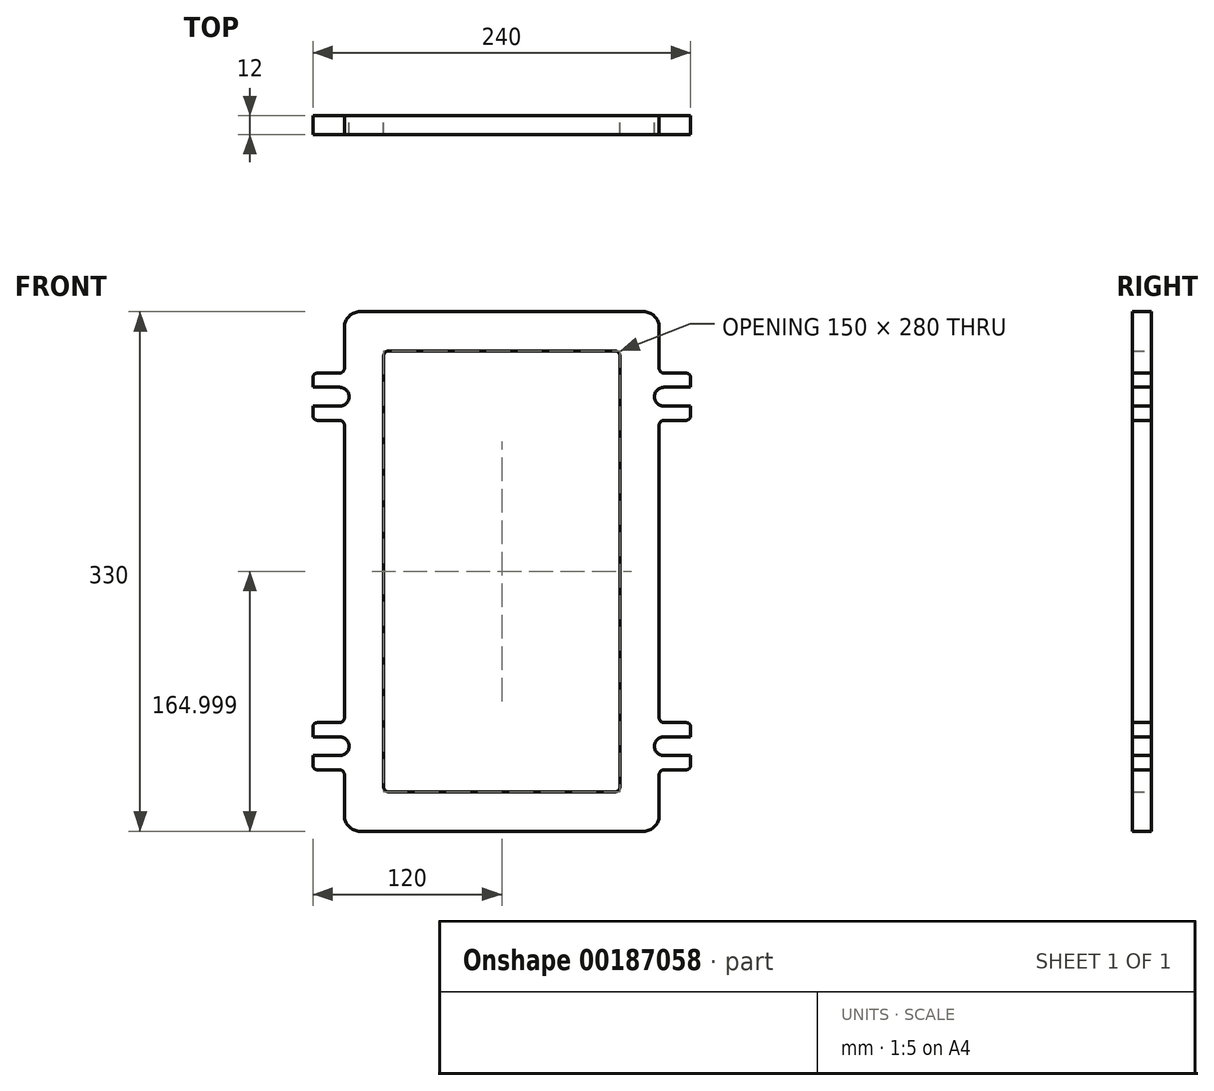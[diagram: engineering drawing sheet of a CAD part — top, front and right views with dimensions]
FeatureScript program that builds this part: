
annotation { "Feature Type Name" : "Feature", "Feature Type Description" : "" }
export const myFeature = defineFeature(function(context is Context, id is Id, definition is map)
    precondition{}
    {
        {
            var Q0;
            Q0=qCreatedBy(makeId("Front.planeOp"),FACE);
            var sketch = newSketch(context, id + "F0", { "sketchPlane" : qUnion([Q0])});
            skLineSegment(sketch, "E0", {"start": v(-100, 111.18) * mm, "end": v(0, 111.18) * mm});
            skLineSegment(sketch, "E1", {"start": v(-100, 111.18) * mm, "end": v(-100, 72.18) * mm});
            skLineSegment(sketch, "E2", {"start": v(-100, 72.18) * mm, "end": v(-120, 72.18) * mm});
            skLineSegment(sketch, "E3", {"start": v(-120, 72.18) * mm, "end": v(-120, 63.18) * mm});
            skLineSegment(sketch, "E4", {"start": v(-120, 63.18) * mm, "end": v(-103, 63.18) * mm});
            skLineSegment(sketch, "E5", {"start": v(-103, 51.18) * mm, "end": v(-120, 51.18) * mm});
            skLineSegment(sketch, "E6", {"start": v(-120, 51.18) * mm, "end": v(-120, 42.18) * mm});
            skLineSegment(sketch, "E7", {"start": v(-120, 42.18) * mm, "end": v(-100, 42.18) * mm});
            skLineSegment(sketch, "E8", {"start": v(-100, 42.18) * mm, "end": v(-100, -53.82) * mm});
            skArc(sketch, "E9", {"start": v(-103, 51.18) * mm, "mid": v(-97, 57.18) * mm, "end": v(-103, 63.18) * mm});
            skLineSegment(sketch, "E10.0", {"start": v(-75, 86.18) * mm, "end": v(0, 86.18) * mm});
            skLineSegment(sketch, "E11.0", {"start": v(-75, 86.18) * mm, "end": v(-75, -53.82) * mm});
            skLineSegment(sketch, "E12.MirrorCS", {"start": v(120, 51.18) * mm, "end": v(120, 42.18) * mm});
            skLineSegment(sketch, "E13.MirrorCS", {"start": v(120, 72.18) * mm, "end": v(120, 63.18) * mm});
            skArc(sketch, "E14.MirrorCS", {"start": v(103, 51.18) * mm, "mid": v(97, 57.18) * mm, "end": v(103, 63.18) * mm});
            skLineSegment(sketch, "E15.MirrorCS", {"start": v(75, 86.18) * mm, "end": v(75, -53.82) * mm});
            skLineSegment(sketch, "E16.MirrorCS", {"start": v(75, 86.18) * mm, "end": v(0, 86.18) * mm});
            skLineSegment(sketch, "E17.MirrorCS", {"start": v(100, 42.18) * mm, "end": v(100, -53.82) * mm});
            skLineSegment(sketch, "E18.MirrorCS", {"start": v(120, 42.18) * mm, "end": v(100, 42.18) * mm});
            skLineSegment(sketch, "E19.MirrorCS", {"start": v(100, 111.18) * mm, "end": v(100, 72.18) * mm});
            skLineSegment(sketch, "E20.MirrorCS", {"start": v(103, 51.18) * mm, "end": v(120, 51.18) * mm});
            skLineSegment(sketch, "E21.MirrorCS", {"start": v(120, 63.18) * mm, "end": v(103, 63.18) * mm});
            skLineSegment(sketch, "E22.MirrorCS", {"start": v(100, 72.18) * mm, "end": v(120, 72.18) * mm});
            skLineSegment(sketch, "E23.MirrorCS", {"start": v(100, 111.18) * mm, "end": v(0, 111.18) * mm});
            skLineSegment(sketch, "E24.MirrorCS", {"start": v(120, -179.82) * mm, "end": v(120, -170.82) * mm});
            skLineSegment(sketch, "E25.MirrorCS", {"start": v(120, -158.82) * mm, "end": v(120, -149.82) * mm});
            skLineSegment(sketch, "E26.MirrorCS", {"start": v(-100, -179.82) * mm, "end": v(-120, -179.82) * mm});
            skArc(sketch, "E27.MirrorCS", {"start": v(-103, -158.82) * mm, "mid": v(-97, -164.82) * mm, "end": v(-103, -170.82) * mm});
            skLineSegment(sketch, "E28.MirrorCS", {"start": v(-103, -158.82) * mm, "end": v(-120, -158.82) * mm});
            skLineSegment(sketch, "E29.MirrorCS", {"start": v(100, -179.82) * mm, "end": v(120, -179.82) * mm});
            skLineSegment(sketch, "E30.MirrorCS", {"start": v(103, -158.82) * mm, "end": v(120, -158.82) * mm});
            skLineSegment(sketch, "E31.MirrorCS", {"start": v(120, -149.82) * mm, "end": v(100, -149.82) * mm});
            skArc(sketch, "E32.MirrorCS", {"start": v(103, -158.82) * mm, "mid": v(97, -164.82) * mm, "end": v(103, -170.82) * mm});
            skLineSegment(sketch, "E33.MirrorCS", {"start": v(-120, -170.82) * mm, "end": v(-103, -170.82) * mm});
            skLineSegment(sketch, "E34.MirrorCS", {"start": v(-120, -149.82) * mm, "end": v(-100, -149.82) * mm});
            skLineSegment(sketch, "E35.MirrorCS", {"start": v(-120, -179.82) * mm, "end": v(-120, -170.82) * mm});
            skLineSegment(sketch, "E36.MirrorCS", {"start": v(-120, -158.82) * mm, "end": v(-120, -149.82) * mm});
            skLineSegment(sketch, "E37.MirrorCS", {"start": v(120, -170.82) * mm, "end": v(103, -170.82) * mm});
            skLineSegment(sketch, "E38.MirrorCS", {"start": v(75, -193.82) * mm, "end": v(75, -53.82) * mm});
            skLineSegment(sketch, "E39.MirrorCS", {"start": v(-100, -218.82) * mm, "end": v(0, -218.82) * mm});
            skLineSegment(sketch, "E40.MirrorCS", {"start": v(-100, -218.82) * mm, "end": v(-100, -179.82) * mm});
            skLineSegment(sketch, "E41.MirrorCS", {"start": v(100, -218.82) * mm, "end": v(0, -218.82) * mm});
            skLineSegment(sketch, "E42.MirrorCS", {"start": v(75, -193.82) * mm, "end": v(0, -193.82) * mm});
            skLineSegment(sketch, "E43.MirrorCS", {"start": v(100, -149.82) * mm, "end": v(100, -53.82) * mm});
            skLineSegment(sketch, "E44.MirrorCS", {"start": v(100, -218.82) * mm, "end": v(100, -179.82) * mm});
            skLineSegment(sketch, "E45.MirrorCS", {"start": v(-75, -193.82) * mm, "end": v(-75, -53.82) * mm});
            skLineSegment(sketch, "E46.MirrorCS", {"start": v(-75, -193.82) * mm, "end": v(0, -193.82) * mm});
            skLineSegment(sketch, "E47.MirrorCS", {"start": v(-100, -149.82) * mm, "end": v(-100, -53.82) * mm});
            skSolve(sketch);
        }
        {
            var Q0;
            Q0 = qSketchRegion(id + "F0", true);
            extrude(context, id + "F1", {"entities" : qUnion([Q0]), "depth" : 12 * mm, "symmetric" : true});
        }
        {
            var Q0;
            Q0=makeQuery(id+"F1.opExtrude","SWEPT_EDGE",EDGE,{"disambiguationData":[OSD([sQuery(id+"F0.wireOp",EDGE,"E19.MirrorCS"),sQuery(id+"F0.wireOp",EDGE,"E23.MirrorCS")])]});
            var Q1;
            Q1=makeQuery(id+"F1.opExtrude","SWEPT_EDGE",EDGE,{"disambiguationData":[OSD([sQuery(id+"F0.wireOp",EDGE,"E0"),sQuery(id+"F0.wireOp",EDGE,"E1")])]});
            var Q2;
            Q2=makeQuery(id+"F1.opExtrude","SWEPT_EDGE",EDGE,{"disambiguationData":[OSD([sQuery(id+"F0.wireOp",EDGE,"E41.MirrorCS"),sQuery(id+"F0.wireOp",EDGE,"E44.MirrorCS")])]});
            var Q3;
            Q3=makeQuery(id+"F1.opExtrude","SWEPT_EDGE",EDGE,{"disambiguationData":[OSD([sQuery(id+"F0.wireOp",EDGE,"E39.MirrorCS"),sQuery(id+"F0.wireOp",EDGE,"E40.MirrorCS")])]});
            fillet(context, id + "F2", {"entities" : qUnion([Q0, Q1, Q2, Q3]), "radius" : 10 * mm, "tangentPropagation" : true, "allowEdgeOverflow" : false});
        }
        {
            var Q0;
            Q0=makeQuery(id+"F1.opExtrude","SWEPT_EDGE",EDGE,{"disambiguationData":[OSD([sQuery(id+"F0.wireOp",EDGE,"E45.MirrorCS"),sQuery(id+"F0.wireOp",EDGE,"E46.MirrorCS")])]});
            var Q1;
            Q1=makeQuery(id+"F1.opExtrude","SWEPT_EDGE",EDGE,{"disambiguationData":[OSD([sQuery(id+"F0.wireOp",EDGE,"E38.MirrorCS"),sQuery(id+"F0.wireOp",EDGE,"E42.MirrorCS")])]});
            var Q2;
            Q2=makeQuery(id+"F1.opExtrude","SWEPT_EDGE",EDGE,{"disambiguationData":[OSD([sQuery(id+"F0.wireOp",EDGE,"E15.MirrorCS"),sQuery(id+"F0.wireOp",EDGE,"E16.MirrorCS")])]});
            var Q3;
            Q3=makeQuery(id+"F1.opExtrude","SWEPT_EDGE",EDGE,{"disambiguationData":[OSD([sQuery(id+"F0.wireOp",EDGE,"E10.0"),sQuery(id+"F0.wireOp",EDGE,"E11.0")])]});
            fillet(context, id + "F3", {"entities" : qUnion([Q0, Q1, Q2, Q3]), "radius" : 3 * mm, "tangentPropagation" : true, "allowEdgeOverflow" : false});
        }
        {
            var Q0;
            Q0=makeQuery(id+"F1.opExtrude","SWEPT_EDGE",EDGE,{"disambiguationData":[OSD([sQuery(id+"F0.wireOp",EDGE,"E34.MirrorCS"),sQuery(id+"F0.wireOp",EDGE,"E36.MirrorCS")])]});
            var Q1;
            Q1=makeQuery(id+"F1.opExtrude","SWEPT_EDGE",EDGE,{"disambiguationData":[OSD([sQuery(id+"F0.wireOp",EDGE,"E26.MirrorCS"),sQuery(id+"F0.wireOp",EDGE,"E35.MirrorCS")])]});
            var Q2;
            Q2=makeQuery(id+"F1.opExtrude","SWEPT_EDGE",EDGE,{"disambiguationData":[OSD([sQuery(id+"F0.wireOp",EDGE,"E25.MirrorCS"),sQuery(id+"F0.wireOp",EDGE,"E31.MirrorCS")])]});
            var Q3;
            Q3=makeQuery(id+"F1.opExtrude","SWEPT_EDGE",EDGE,{"disambiguationData":[OSD([sQuery(id+"F0.wireOp",EDGE,"E24.MirrorCS"),sQuery(id+"F0.wireOp",EDGE,"E29.MirrorCS")])]});
            var Q4;
            Q4=makeQuery(id+"F1.opExtrude","SWEPT_EDGE",EDGE,{"disambiguationData":[OSD([sQuery(id+"F0.wireOp",EDGE,"E13.MirrorCS"),sQuery(id+"F0.wireOp",EDGE,"E22.MirrorCS")])]});
            var Q5;
            Q5=makeQuery(id+"F1.opExtrude","SWEPT_EDGE",EDGE,{"disambiguationData":[OSD([sQuery(id+"F0.wireOp",EDGE,"E12.MirrorCS"),sQuery(id+"F0.wireOp",EDGE,"E18.MirrorCS")])]});
            var Q6;
            Q6=makeQuery(id+"F1.opExtrude","SWEPT_EDGE",EDGE,{"disambiguationData":[OSD([sQuery(id+"F0.wireOp",EDGE,"E2"),sQuery(id+"F0.wireOp",EDGE,"E3")])]});
            var Q7;
            Q7=makeQuery(id+"F1.opExtrude","SWEPT_EDGE",EDGE,{"disambiguationData":[OSD([sQuery(id+"F0.wireOp",EDGE,"E6"),sQuery(id+"F0.wireOp",EDGE,"E7")])]});
            fillet(context, id + "F4", {"entities" : qUnion([Q0, Q1, Q2, Q3, Q4, Q5, Q6, Q7]), "radius" : 3 * mm, "tangentPropagation" : true, "allowEdgeOverflow" : false});
        }
        {
            var Q0;
            Q0=makeQuery(id+"F1.opExtrude","SWEPT_EDGE",EDGE,{"disambiguationData":[OSD([sQuery(id+"F0.wireOp",EDGE,"E19.MirrorCS"),sQuery(id+"F0.wireOp",EDGE,"E22.MirrorCS")])]});
            var Q1;
            Q1=makeQuery(id+"F1.opExtrude","SWEPT_EDGE",EDGE,{"disambiguationData":[OSD([sQuery(id+"F0.wireOp",EDGE,"E17.MirrorCS"),sQuery(id+"F0.wireOp",EDGE,"E18.MirrorCS")])]});
            var Q2;
            Q2=makeQuery(id+"F1.opExtrude","SWEPT_EDGE",EDGE,{"disambiguationData":[OSD([sQuery(id+"F0.wireOp",EDGE,"E29.MirrorCS"),sQuery(id+"F0.wireOp",EDGE,"E44.MirrorCS")])]});
            var Q3;
            Q3=makeQuery(id+"F1.opExtrude","SWEPT_EDGE",EDGE,{"disambiguationData":[OSD([sQuery(id+"F0.wireOp",EDGE,"E31.MirrorCS"),sQuery(id+"F0.wireOp",EDGE,"E43.MirrorCS")])]});
            var Q4;
            Q4=makeQuery(id+"F1.opExtrude","SWEPT_EDGE",EDGE,{"disambiguationData":[OSD([sQuery(id+"F0.wireOp",EDGE,"E34.MirrorCS"),sQuery(id+"F0.wireOp",EDGE,"E47.MirrorCS")])]});
            var Q5;
            Q5=makeQuery(id+"F1.opExtrude","SWEPT_EDGE",EDGE,{"disambiguationData":[OSD([sQuery(id+"F0.wireOp",EDGE,"E26.MirrorCS"),sQuery(id+"F0.wireOp",EDGE,"E40.MirrorCS")])]});
            var Q6;
            Q6=makeQuery(id+"F1.opExtrude","SWEPT_EDGE",EDGE,{"disambiguationData":[OSD([sQuery(id+"F0.wireOp",EDGE,"E1"),sQuery(id+"F0.wireOp",EDGE,"E2")])]});
            var Q7;
            Q7=makeQuery(id+"F1.opExtrude","SWEPT_EDGE",EDGE,{"disambiguationData":[OSD([sQuery(id+"F0.wireOp",EDGE,"E7"),sQuery(id+"F0.wireOp",EDGE,"E8")])]});
            fillet(context, id + "F5", {"entities" : qUnion([Q0, Q1, Q2, Q3, Q4, Q5, Q6, Q7]), "radius" : 3 * mm, "tangentPropagation" : true, "allowEdgeOverflow" : false});
        }
    });
